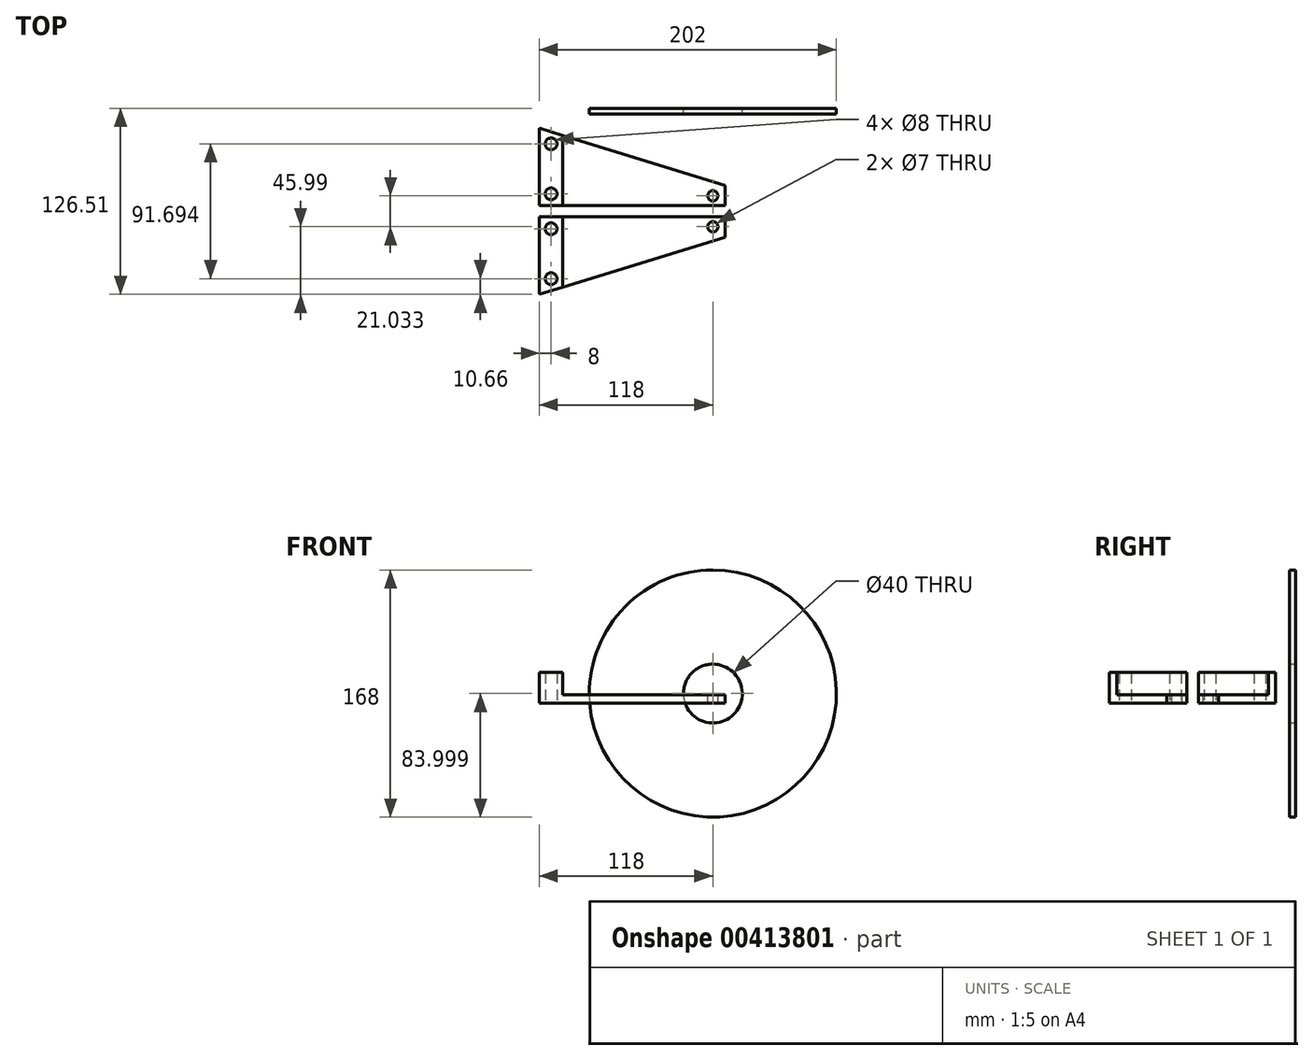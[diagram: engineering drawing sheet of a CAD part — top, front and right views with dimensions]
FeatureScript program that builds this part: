
annotation { "Feature Type Name" : "Feature", "Feature Type Description" : "" }
export const myFeature = defineFeature(function(context is Context, id is Id, definition is map)
    precondition{}
    {
        {
            var Q0;
            Q0=qCreatedBy(makeId("Front.planeOp"),FACE);
            var sketch = newSketch(context, id + "F0", { "sketchPlane" : qUnion([Q0])});
            skCircle(sketch, "E0", {"center": v(118, 6.67) * mm, "radius": 3.5 * mm});
            skCircle(sketch, "E1", {"center": v(8, 42) * mm, "radius": 4 * mm});
            skCircle(sketch, "E2", {"center": v(8, 8) * mm, "radius": 4 * mm});
            skPoint(sketch, "E3", {"position": v(8, 46) * mm});
            skPoint(sketch, "E4", {"position": v(4, 42) * mm});
            skPoint(sketch, "E5", {"position": v(8, 4) * mm});
            skLineSegment(sketch, "E6", {"start": v(0, 0) * mm, "end": v(126.5, 0) * mm});
            skLineSegment(sketch, "E7", {"start": v(126.5, 0) * mm, "end": v(126.5, 13.84) * mm});
            skLineSegment(sketch, "E8", {"start": v(126.5, 13.84) * mm, "end": v(0, 52.66) * mm});
            skLineSegment(sketch, "E9", {"start": v(0, 52.66) * mm, "end": v(0, 0) * mm});
            skLineSegment(sketch, "E10", {"start": v(16, 47.75) * mm, "end": v(16, 0) * mm});
            skPoint(sketch, "E11", {"position": v(121.5, 6.67) * mm});
            skPoint(sketch, "E12", {"position": v(118, 10.17) * mm});
            skSolve(sketch);
        }
        {
            var Q0;
            Q0=makeQuery(id+"F0.imprint","IMPRINT",FACE,{"disambiguationData":[TD([[makeQuery(id+"F0.imprint","IMPRINT",EDGE,{"derivedFrom":sQuery(id+"F0.wireOp",EDGE,"iUGU7pFC-bX2C-A5NQ-ZXcU-o8NXg60gN6pC.bottom")}),1.0]])]});
            var Q1;
            Q1=makeQuery(id+"F0.imprint","IMPRINT",FACE,{"disambiguationData":[TD([[makeQuery(id+"F0.imprint","IMPRINT",EDGE,{"derivedFrom":sQuery(id+"F0.wireOp",EDGE,"0t4u72Rh-4CgE-xCGx-8RAQ-GXC0zO71v9mb.bottom")}),1.0]])]});
            var Q2;
            Q2=makeQuery(id+"F0.imprint","IMPRINT",FACE,{"disambiguationData":[TD([[makeQuery(id+"F0.imprint","IMPRINT",EDGE,{"derivedFrom":sQuery(id+"F0.wireOp",EDGE,"E0")}),-1.0]])]});
            extrude(context, id + "F1", {"entities" : qUnion([Q0, Q1, Q2]), "endBound" : BoundingType.SYMMETRIC, "depth" : 6 * mm});
        }
        {
            var Q0;
            Q0=sQuery(id+"F0.wireOp",VERTEX,"E0.center");
            var Q1;
            Q1=qCreatedBy(makeId("Top.planeOp"),FACE);
            cPlane(context, id + "F2", {"entities" : qUnion([Q0, Q1]), "cplaneType" : CPlaneType.PLANE_POINT, "offset" : 25 * mm, "width" : 150 * mm, "height" : 150 * mm});
        }
        {
            var Q0;
            Q0=qCreatedBy(id+"F2.planeOp",FACE);
            var sketch = newSketch(context, id + "F3", { "sketchPlane" : qUnion([Q0])});
            skLineSegment(sketch, "E13.bottom", {"start": v(138, 14.85) * mm, "end": v(202, 14.85) * mm});
            skLineSegment(sketch, "E13.top", {"start": v(138, 10.85) * mm, "end": v(202, 10.85) * mm});
            skLineSegment(sketch, "E13.left", {"start": v(138, 14.85) * mm, "end": v(138, 10.85) * mm});
            skLineSegment(sketch, "E13.right", {"start": v(202, 14.85) * mm, "end": v(202, 10.85) * mm});
            skLineSegment(sketch, "E14.bottom", {"start": v(138, 14.85) * mm, "end": v(181.8, 14.85) * mm});
            skLineSegment(sketch, "E14.top", {"start": v(138, 66.85) * mm, "end": v(181.8, 66.85) * mm});
            skLineSegment(sketch, "E14.left", {"start": v(138, 14.85) * mm, "end": v(138, 66.85) * mm});
            skLineSegment(sketch, "E14.right", {"start": v(181.8, 14.85) * mm, "end": v(181.8, 66.85) * mm});
            skLineSegment(sketch, "E15.bottom", {"start": v(138, 66.85) * mm, "end": v(202, 66.85) * mm});
            skLineSegment(sketch, "E15.top", {"start": v(138, 70.85) * mm, "end": v(202, 70.85) * mm});
            skLineSegment(sketch, "E15.left", {"start": v(138, 66.85) * mm, "end": v(138, 70.85) * mm});
            skLineSegment(sketch, "E15.right", {"start": v(202, 66.85) * mm, "end": v(202, 70.85) * mm});
            skLineSegment(sketch, "E16", {"start": v(236.77, 40.85) * mm, "end": v(285.48, 40.85) * mm, "construction": true});
            skPoint(sketch, "E16.startSnap0", {"position": v(181.8, 40.85) * mm});
            skPoint(sketch, "E16.endSnap0", {"position": v(181.8, 40.85) * mm});
            skPoint(sketch, "E17", {"position": v(0, 40.85) * mm});
            skPoint(sketch, "E17.positionSnap0", {"position": v(118, 40.85) * mm});
            skLineSegment(sketch, "E18", {"start": v(118, 40.85) * mm, "end": v(118, 34.85) * mm, "construction": true});
            skPoint(sketch, "E19", {"position": v(138, 40.85) * mm});
            skSolve(sketch);
        }
        {
            var Q0;
            Q0=makeQuery(id+"F3.imprint","IMPRINT",FACE,{"disambiguationData":[TD([[makeQuery(id+"F3.imprint","IMPRINT",EDGE,{"derivedFrom":sQuery(id+"F3.wireOp",EDGE,"E14.bottom")}),1.0]])]});
            var Q1;
            Q1=makeQuery(id+"F3.imprint","IMPRINT",FACE,{"disambiguationData":[TD([[makeQuery(id+"F3.imprint","IMPRINT",EDGE,{"derivedFrom":sQuery(id+"F3.wireOp",EDGE,"E13.bottom")}),-1.0]])]});
            var Q2;
            Q2=makeQuery(id+"F3.imprint","IMPRINT",FACE,{"disambiguationData":[TD([[makeQuery(id+"F3.imprint","IMPRINT",EDGE,{"derivedFrom":sQuery(id+"F3.wireOp",EDGE,"E15.top")}),-1.0]])]});
            var Q3;
            Q3=sQuery(id+"F3.wireOp",EDGE,"E18");
            revolve(context, id + "F4", {"entities" : qUnion([Q0, Q1, Q2]), "axis" : qUnion([Q3]), "revolveType" : RevolveType.FULL});
        }
        {
            var Q0;
            Q0=makeQuery(id+"F0.imprint","IMPRINT",FACE,{"disambiguationData":[TD([[makeQuery(id+"F0.imprint","IMPRINT",EDGE,{"derivedFrom":sQuery(id+"F0.wireOp",EDGE,"E1")}),-1.0]])]});
            var Q1;
            Q1=makeQuery(id+"F1.opExtrude","CAP_FACE",FACE,{"disambiguationData":[OSD([sQuery(id+"F0.wireOp",EDGE,"E0"),sQuery(id+"F0.wireOp",EDGE,"E6"),sQuery(id+"F0.wireOp",EDGE,"E7"),sQuery(id+"F0.wireOp",EDGE,"E8"),sQuery(id+"F0.wireOp",EDGE,"E10")])],"isStart":false});
            extrude(context, id + "F5", {"entities" : qUnion([Q0]), "operationType" : NewBodyOperationType.ADD, "oppositeDirection" : true, "depth" : 18 * mm, "hasSecondDirection" : true, "secondDirectionBound" : SecondDirectionBoundingType.UP_TO_SURFACE, "secondDirectionOppositeDirection" : false, "secondDirectionBoundEntityFace" : qUnion([Q1]), "secondDirectionDepth" : 5 * mm});
        }
        {
            var Q0;
            Q0=qCreatedBy(makeId("Front.planeOp"),FACE);
            var Q1;
            Q1=sQuery(id+"F3.wireOp",VERTEX,"E17");
            cPlane(context, id + "F6", {"entities" : qUnion([Q0, Q1]), "cplaneType" : CPlaneType.PLANE_POINT, "offset" : 25 * mm, "oppositeDirection" : true, "width" : 150 * mm, "height" : 150 * mm});
        }
        {
            var Q0;
            Q0=makeQuery(id+"F1.opExtrude","SWEPT_BODY",BODY,{"disambiguationData":[OSD([sQuery(id+"F0.wireOp",EDGE,"E0"),sQuery(id+"F0.wireOp",EDGE,"E6"),sQuery(id+"F0.wireOp",EDGE,"E7"),sQuery(id+"F0.wireOp",EDGE,"E8"),sQuery(id+"F0.wireOp",EDGE,"E10")])]});
            var Q1;
            Q1=qCreatedBy(id+"F6.planeOp",FACE);
            mirror(context, id + "F7", {"entities" : qUnion([Q0]), "mirrorPlane" : qUnion([Q1])});
        }
        {
            var Q0;
            Q0=makeQuery(id+"F1.opExtrude","SWEPT_BODY",BODY,{"disambiguationData":[OSD([sQuery(id+"F0.wireOp",EDGE,"E0"),sQuery(id+"F0.wireOp",EDGE,"E6"),sQuery(id+"F0.wireOp",EDGE,"E7"),sQuery(id+"F0.wireOp",EDGE,"E8"),sQuery(id+"F0.wireOp",EDGE,"E10")])]});
            var Q1;
            {var subQ0=sQuery(id+"F0.wireOp",EDGE,"E10");var subQ1=sQuery(id+"F0.wireOp",EDGE,"E6");Q1=makeQuery(id+"F5.boolean.opBoolean","MERGE",EDGE,{"derivedFrom":[makeQuery(id+"F1.opExtrude","CAP_EDGE",EDGE,{"disambiguationData":[OSD([subQ1])],"isStart":false}),makeQuery(id+"F5.opExtrude","TWEAK_EDGE",EDGE,{"derivedFrom":[makeQuery(id+"F0.imprint","IMPRINT",EDGE,{"disambiguationData":[TD([[makeQuery(id+"F0.imprint","INTERSECT",VERTEX,{"derivedFrom":[subQ1,sQuery(id+"F0.wireOp",EDGE,"E9")]}),-1.0]])],"derivedFrom":subQ1}),makeQuery(id+"F1.opExtrude","CAP_FACE",FACE,{"disambiguationData":[OSD([sQuery(id+"F0.wireOp",EDGE,"E0"),subQ1,sQuery(id+"F0.wireOp",EDGE,"E7"),sQuery(id+"F0.wireOp",EDGE,"E8"),subQ0])],"isStart":false})]})]});}
            var Q2;
            {var subQ0=sQuery(id+"F0.wireOp",EDGE,"E10");var subQ1=sQuery(id+"F0.wireOp",EDGE,"E6");Q2=makeQuery(id+"F5.boolean.opBoolean","MERGE",EDGE,{"derivedFrom":[makeQuery(id+"F1.opExtrude","CAP_EDGE",EDGE,{"disambiguationData":[OSD([subQ1])],"isStart":false}),makeQuery(id+"F5.opExtrude","TWEAK_EDGE",EDGE,{"derivedFrom":[makeQuery(id+"F0.imprint","IMPRINT",EDGE,{"disambiguationData":[TD([[makeQuery(id+"F0.imprint","INTERSECT",VERTEX,{"derivedFrom":[subQ1,sQuery(id+"F0.wireOp",EDGE,"E9")]}),-1.0]])],"derivedFrom":subQ1}),makeQuery(id+"F1.opExtrude","CAP_FACE",FACE,{"disambiguationData":[OSD([sQuery(id+"F0.wireOp",EDGE,"E0"),subQ1,sQuery(id+"F0.wireOp",EDGE,"E7"),sQuery(id+"F0.wireOp",EDGE,"E8"),subQ0])],"isStart":false})]})]});}
            transform(context, id + "F8", {"entities" : qUnion([Q0]), "transformType" : TransformType.ROTATION, "transformAxis" : qUnion([Q2]), "angle" : 90 * degree, "makeCopy" : false});
        }
        {
            var Q0;
            Q0=makeQuery(id+"F7.opPattern","COPY",BODY,{"derivedFrom":makeQuery(id+"F1.opExtrude","SWEPT_BODY",BODY,{"disambiguationData":[OSD([sQuery(id+"F0.wireOp",EDGE,"E0"),sQuery(id+"F0.wireOp",EDGE,"E6"),sQuery(id+"F0.wireOp",EDGE,"E7"),sQuery(id+"F0.wireOp",EDGE,"E8"),sQuery(id+"F0.wireOp",EDGE,"E10")])]}),"instanceName":"1"});
            var Q1;
            {var subQ0=sQuery(id+"F0.wireOp",EDGE,"E10");var subQ1=sQuery(id+"F0.wireOp",EDGE,"E6");Q1=makeQuery(id+"F7.opPattern","COPY",EDGE,{"derivedFrom":makeQuery(id+"F5.boolean.opBoolean","MERGE",EDGE,{"derivedFrom":[makeQuery(id+"F1.opExtrude","CAP_EDGE",EDGE,{"disambiguationData":[OSD([subQ1])],"isStart":false}),makeQuery(id+"F5.opExtrude","TWEAK_EDGE",EDGE,{"derivedFrom":[makeQuery(id+"F0.imprint","IMPRINT",EDGE,{"disambiguationData":[TD([[makeQuery(id+"F0.imprint","INTERSECT",VERTEX,{"derivedFrom":[subQ1,sQuery(id+"F0.wireOp",EDGE,"E9")]}),-1.0]])],"derivedFrom":subQ1}),makeQuery(id+"F1.opExtrude","CAP_FACE",FACE,{"disambiguationData":[OSD([sQuery(id+"F0.wireOp",EDGE,"E0"),subQ1,sQuery(id+"F0.wireOp",EDGE,"E7"),sQuery(id+"F0.wireOp",EDGE,"E8"),subQ0])],"isStart":false})]})]}),"instanceName":"1"});}
            transform(context, id + "F9", {"entities" : qUnion([Q0]), "transformType" : TransformType.ROTATION, "transformAxis" : qUnion([Q1]), "angle" : 90 * degree, "oppositeDirection" : true, "makeCopy" : false});
        }
        {
            var Q0;
            Q0=makeQuery(id+"F7.opPattern","COPY",BODY,{"derivedFrom":makeQuery(id+"F1.opExtrude","SWEPT_BODY",BODY,{"disambiguationData":[OSD([sQuery(id+"F0.wireOp",EDGE,"E0"),sQuery(id+"F0.wireOp",EDGE,"E6"),sQuery(id+"F0.wireOp",EDGE,"E7"),sQuery(id+"F0.wireOp",EDGE,"E8"),sQuery(id+"F0.wireOp",EDGE,"E10")])]}),"instanceName":"1"});
            var Q1;
            Q1=makeQuery(id+"F0.imprint","IMPRINT",FACE,{"disambiguationData":[TD([[makeQuery(id+"F0.imprint","IMPRINT",EDGE,{"derivedFrom":sQuery(id+"F0.wireOp",EDGE,"E1")}),-1.0]])]});
            transform(context, id + "F10", {"entities" : qUnion([Q0]), "transformType" : TransformType.TRANSLATION_3D, "dx" : 0 * mm, "dy" : -80 * mm, "dz" : 0 * mm, "makeCopy" : false});
        }
        {
            var Q0;
            Q0=makeQuery(id+"F4.opRevolve","SWEPT_BODY",BODY,{"disambiguationData":[OSD([sQuery(id+"F3.wireOp",EDGE,"E13.bottom"),sQuery(id+"F3.wireOp",EDGE,"E13.top"),sQuery(id+"F3.wireOp",EDGE,"E13.left"),sQuery(id+"F3.wireOp",EDGE,"E13.right"),sQuery(id+"F3.wireOp",EDGE,"E14.left"),sQuery(id+"F3.wireOp",EDGE,"E14.right"),sQuery(id+"F3.wireOp",EDGE,"E15.bottom"),sQuery(id+"F3.wireOp",EDGE,"E15.top"),sQuery(id+"F3.wireOp",EDGE,"E15.left"),sQuery(id+"F3.wireOp",EDGE,"E15.right")])]});
            deleteBodies(context, id + "F11", {"entities" : qUnion([Q0])});
        }
    });
